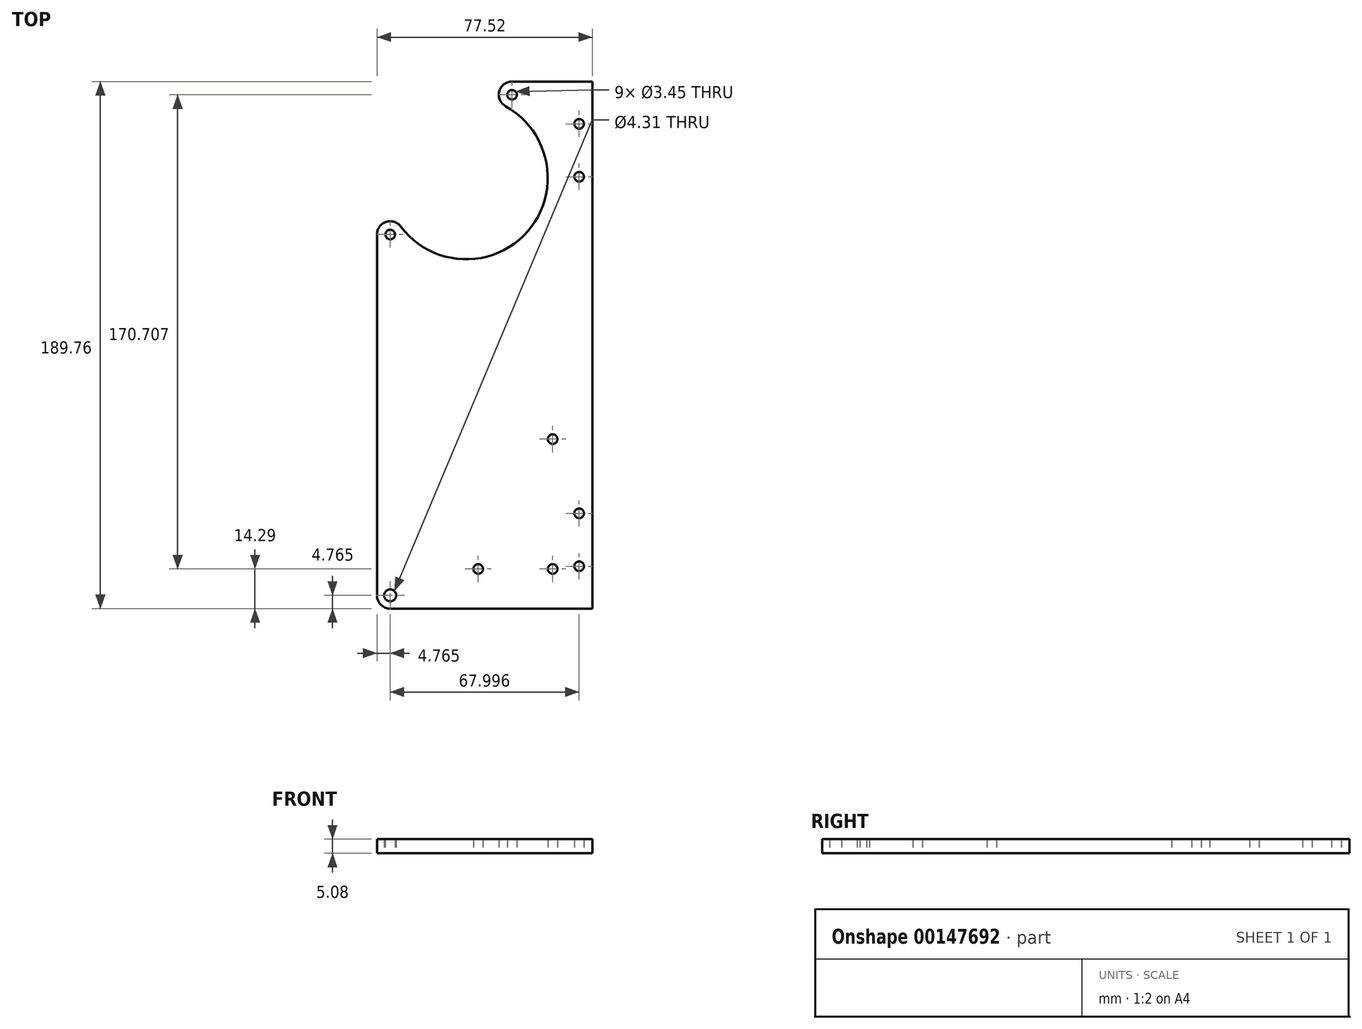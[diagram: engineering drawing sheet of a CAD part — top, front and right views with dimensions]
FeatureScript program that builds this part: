
annotation { "Feature Type Name" : "Feature", "Feature Type Description" : "" }
export const myFeature = defineFeature(function(context is Context, id is Id, definition is map)
    precondition{}
    {
        {
            var Q0;
            Q0=qCreatedBy(makeId("Top.planeOp"),FACE);
            var sketch = newSketch(context, id + "F0", { "sketchPlane" : qUnion([Q0])});
            skLineSegment(sketch, "E0.bottom", {"start": v(45.42, -155.13) * mm, "end": v(-27.34, -155.13) * mm});
            skLineSegment(sketch, "E1", {"start": v(40.66, -155.13) * mm, "end": v(40.66, -139.89) * mm, "construction": true});
            skLineSegment(sketch, "E2", {"start": v(40.66, -139.89) * mm, "end": v(40.66, -120.84) * mm, "construction": true});
            skLineSegment(sketch, "E3", {"start": v(40.66, 34.63) * mm, "end": v(40.66, 19.39) * mm, "construction": true});
            skLineSegment(sketch, "E4", {"start": v(40.66, 19.39) * mm, "end": v(40.66, 0.34) * mm, "construction": true});
            skCircle(sketch, "E5", {"center": v(40.66, 19.39) * mm, "radius": 1.73 * mm});
            skCircle(sketch, "E6", {"center": v(40.66, 0.34) * mm, "radius": 1.73 * mm});
            skCircle(sketch, "E7", {"center": v(40.66, -120.84) * mm, "radius": 1.73 * mm});
            skCircle(sketch, "E8", {"center": v(40.66, -139.89) * mm, "radius": 1.73 * mm});
            skArc(sketch, "E9", {"start": v(-32.1, -150.37) * mm, "mid": v(-30.7, -153.73) * mm, "end": v(-27.34, -155.13) * mm});
            skLineSegment(sketch, "E10", {"start": v(45.42, 34.63) * mm, "end": v(45.42, -155.13) * mm});
            skLineSegment(sketch, "E11", {"start": v(-32.1, -150.37) * mm, "end": v(-32.1, -20.44) * mm});
            skLineSegment(sketch, "E12", {"start": v(45.42, 34.63) * mm, "end": v(16.52, 34.63) * mm});
            skArc(sketch, "E13", {"start": v(16.52, 34.63) * mm, "mid": v(11.9, 31.06) * mm, "end": v(14.22, 25.7) * mm});
            skArc(sketch, "E14", {"start": v(-23.52, -17.59) * mm, "mid": v(-28.84, -15.92) * mm, "end": v(-32.1, -20.44) * mm});
            skArc(sketch, "E15", {"start": v(-23.52, -17.59) * mm, "mid": v(22.14, -19.3) * mm, "end": v(14.22, 25.7) * mm});
            skCircle(sketch, "E16", {"center": v(-27.34, -20.44) * mm, "radius": 1.73 * mm});
            skCircle(sketch, "E17", {"center": v(16.52, 29.87) * mm, "radius": 1.73 * mm});
            skCircle(sketch, "E18", {"center": v(-27.34, -150.37) * mm, "radius": 2.15 * mm});
            skLineSegment(sketch, "E19", {"start": v(45.42, -140.84) * mm, "end": v(31.14, -140.84) * mm, "construction": true});
            skLineSegment(sketch, "E20", {"start": v(31.14, -140.84) * mm, "end": v(31.14, -94.11) * mm, "construction": true});
            skLineSegment(sketch, "E21", {"start": v(31.14, -140.84) * mm, "end": v(4.34, -140.84) * mm, "construction": true});
            skLineSegment(sketch, "E22", {"start": v(31.14, -140.84) * mm, "end": v(31.14, -155.13) * mm, "construction": true});
            skCircle(sketch, "E23", {"center": v(4.34, -140.84) * mm, "radius": 1.73 * mm});
            skCircle(sketch, "E24", {"center": v(31.14, -94.11) * mm, "radius": 1.73 * mm});
            skCircle(sketch, "E25", {"center": v(31.14, -140.84) * mm, "radius": 1.73 * mm});
            skSolve(sketch);
        }
        {
            var Q0;
            Q0=qSketchRegion(id+"F0",true);
            extrude(context, id + "F1", {"entities" : qUnion([Q0]), "depth" : 5.08 * mm});
        }
    });
